# Revit family: Zumtobel PANOS3 R R100
name_source: partatom
category: Lighting Fixtures
revit_build: Autodesk Revit 2018 (Build: 20170223_1515(x64)
units: mm (PartAtom-declared; Revit-internal decimal feet)

## family parameters
Cut with Voids When Loaded = No
Host = Face
Light Source = Yes
OmniClass Number = 23.80.70.11
OmniClass Title = Luminaries for Internal Lighting
Part Type = Normal
Room Calculation Point = No
Round Connector Dimension = Use Diameter
Shared = No

## types (4) — shared parameters
Apparent Load = 8 VA
Assembly Code = D5020200
Body = ZG_Metal_White
Color Filter = 16777215
Description = LED ceiling-recessed luminaire
Dimming Lamp Color Temperature Shift = <None>
Emit Shape Visible in Rendering = Yes
Lamp = LED
Manufacturer = Zumtobel Lighting
Reflector = ZG_Metal_White_Self_Illumination
Tilt Angle = -90.00°
URL = http://www.zumtobel.com
Voltage = 230 V
zero-valued in all types: Default Elevation

## per-type parameters (varying)
| type | Cover Diameter | Cutout Diameter | Emit from Circle Diameter | Height | Length | Model | Photometric Web File | R100H | R100L | WH | Width |
| PANOS3 R R100H TL | 109 mm | 88 mm | 109 mm | 105 mm | 100 mm  [stored 0.328084 ft] | 60819280 | 60819280_(STD).IES | Yes | No | No | 100 mm  [stored 0.328084 ft] |
| PANOS3 R R100H WH | 113 mm | 100 mm  [stored 0.328084 ft] | 113 mm | 105 mm | 109 mm | 60819279 | 60819279_(STD).IES | Yes | No | Yes | 109 mm |
| PANOS3 R R100L TL | 113 mm | 88 mm | 113 mm | 81 mm  [stored 0.265748 ft] | 100 mm  [stored 0.328084 ft] | 60819283 | 60819283_(STD).IES | No | Yes | No | 100 mm  [stored 0.328084 ft] |
| PANOS3 R R100L WH | 109 mm | 100 mm  [stored 0.328084 ft] | 109 mm | 81 mm  [stored 0.265748 ft] | 109 mm | 60819241 | 60819241_(STD).IES | No | Yes | Yes | 109 mm |

note: [stored X ft] marks values corroborated as IEEE doubles in the binary element streams (Revit-internal decimal feet)

## geometry (parser evidence)
native form markers: Sweep x3
no freeform markers — native parametric forms only
